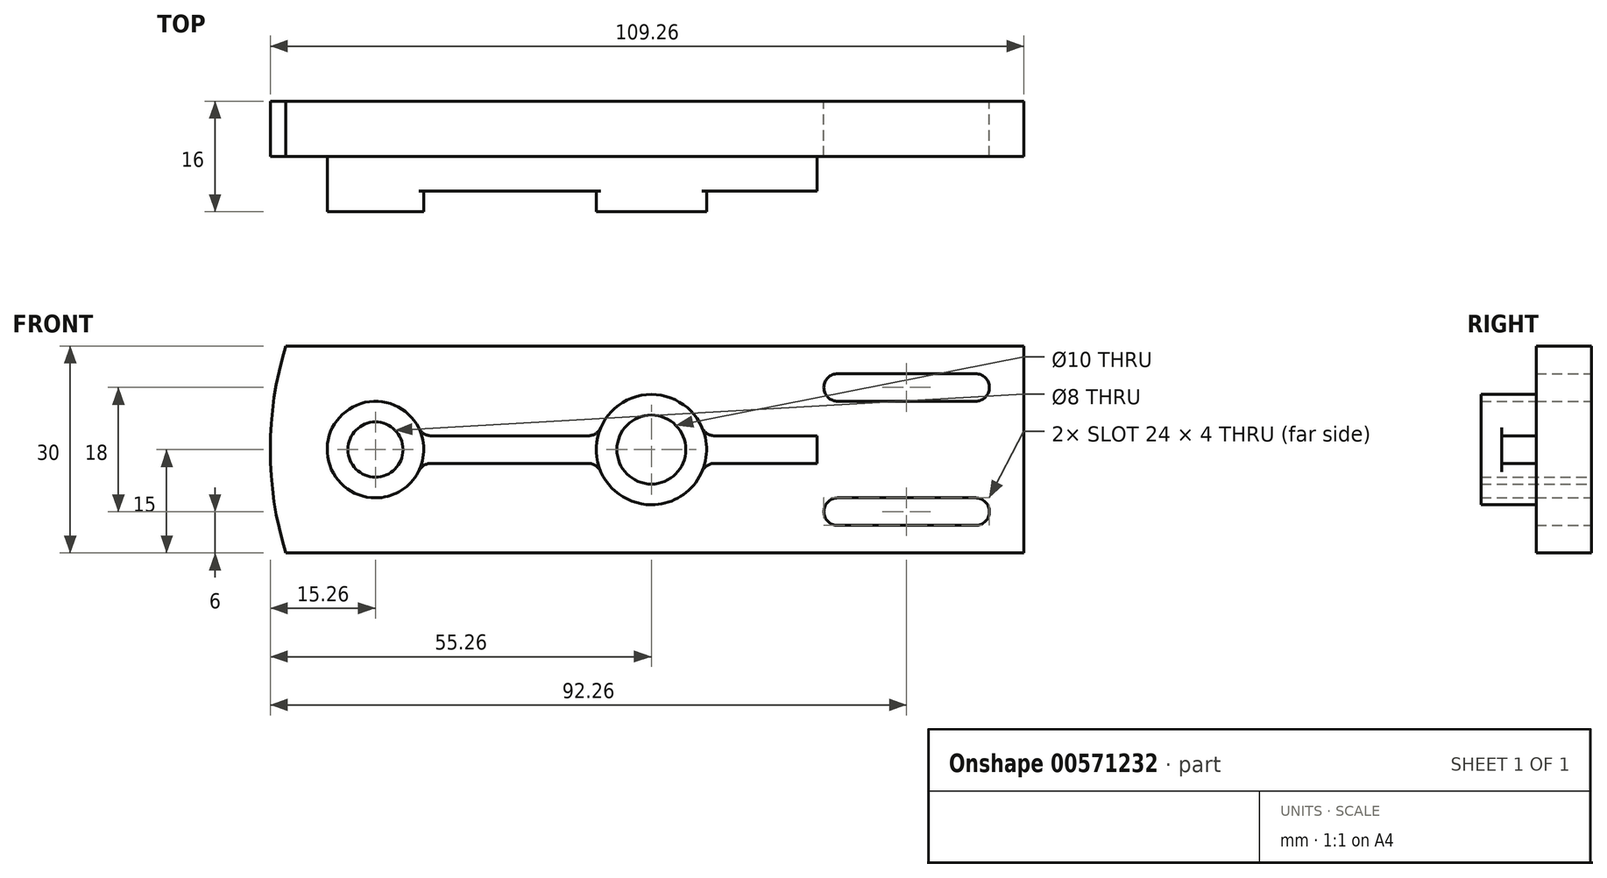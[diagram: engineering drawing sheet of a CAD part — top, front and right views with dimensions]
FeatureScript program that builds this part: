
annotation { "Feature Type Name" : "Feature", "Feature Type Description" : "" }
export const myFeature = defineFeature(function(context is Context, id is Id, definition is map)
    precondition{}
    {
        {
            var Q0;
            Q0=qCreatedBy(makeId("Front.planeOp"),FACE);
            var sketch = newSketch(context, id + "F0", { "sketchPlane" : qUnion([Q0])});
            skLineSegment(sketch, "E0", {"start": v(0, 0) * mm, "end": v(107, 0) * mm});
            skLineSegment(sketch, "E1", {"start": v(107, 0) * mm, "end": v(107, -30) * mm});
            skLineSegment(sketch, "E2", {"start": v(107, -30) * mm, "end": v(0, -30) * mm});
            skArc(sketch, "E3", {"start": v(0, 0) * mm, "mid": v(-2.26, -15) * mm, "end": v(0, -30) * mm});
            skLineSegment(sketch, "E4", {"start": v(-2.26, -15) * mm, "end": v(107, -15) * mm, "construction": true});
            skLineSegment(sketch, "E5", {"start": v(80, -4) * mm, "end": v(100, -4) * mm});
            skLineSegment(sketch, "E6", {"start": v(80, -8) * mm, "end": v(100, -8) * mm});
            skArc(sketch, "E7", {"start": v(100, -8) * mm, "mid": v(102, -6) * mm, "end": v(100, -4) * mm});
            skArc(sketch, "E8", {"start": v(80, -4) * mm, "mid": v(78, -6) * mm, "end": v(80, -8) * mm});
            skLineSegment(sketch, "E9", {"start": v(80, -22) * mm, "end": v(100, -22) * mm});
            skLineSegment(sketch, "E10", {"start": v(80, -26) * mm, "end": v(100, -26) * mm});
            skArc(sketch, "E11", {"start": v(100, -26) * mm, "mid": v(102, -24) * mm, "end": v(100, -22) * mm});
            skArc(sketch, "E12", {"start": v(80, -22) * mm, "mid": v(78, -24) * mm, "end": v(80, -26) * mm});
            skCircle(sketch, "E13", {"center": v(53, -15) * mm, "radius": 5 * mm});
            skCircle(sketch, "E14", {"center": v(13, -15) * mm, "radius": 4 * mm});
            skCircle(sketch, "E15", {"center": v(13, -15) * mm, "radius": 7 * mm});
            skCircle(sketch, "E16", {"center": v(53, -15) * mm, "radius": 8 * mm});
            skLineSegment(sketch, "E17.bottom", {"start": v(62.17, -13) * mm, "end": v(77, -13) * mm});
            skLineSegment(sketch, "E17.top", {"start": v(62.17, -17) * mm, "end": v(77, -17) * mm});
            skLineSegment(sketch, "E17.right", {"start": v(77, -13) * mm, "end": v(77, -17) * mm});
            skLineSegment(sketch, "E18", {"start": v(43.83, -13) * mm, "end": v(21.06, -13) * mm});
            skLineSegment(sketch, "E19", {"start": v(43.83, -17) * mm, "end": v(21.06, -17) * mm});
            skArc(sketch, "E20", {"start": v(19.27, -11.89) * mm, "mid": v(20, -12.7) * mm, "end": v(21.06, -13) * mm});
            skArc(sketch, "E21", {"start": v(21.06, -17) * mm, "mid": v(20, -17.3) * mm, "end": v(19.27, -18.11) * mm});
            skArc(sketch, "E22", {"start": v(43.83, -13) * mm, "mid": v(44.93, -12.67) * mm, "end": v(45.67, -11.8) * mm});
            skArc(sketch, "E23", {"start": v(60.33, -11.8) * mm, "mid": v(61.07, -12.67) * mm, "end": v(62.17, -13) * mm});
            skArc(sketch, "E24", {"start": v(62.17, -17) * mm, "mid": v(61.07, -17.33) * mm, "end": v(60.33, -18.2) * mm});
            skArc(sketch, "E25", {"start": v(45.67, -18.2) * mm, "mid": v(44.93, -17.33) * mm, "end": v(43.83, -17) * mm});
            skPoint(sketch, "E26.orphan", {"position": v(45.25, -13) * mm});
            skPoint(sketch, "E27.orphan", {"position": v(45.25, -17) * mm});
            skPoint(sketch, "E28.orphan", {"position": v(60.75, -13) * mm});
            skPoint(sketch, "E29.orphan", {"position": v(60.75, -17) * mm});
            skSolve(sketch);
        }
        {
            var Q0;
            Q0=makeQuery(id+"F0.imprint","IMPRINT",FACE,{"disambiguationData":[TD([[makeQuery(id+"F0.imprint","IMPRINT",EDGE,{"derivedFrom":sQuery(id+"F0.wireOp",EDGE,"E0")}),-1.0]])]});
            extrude(context, id + "F1", {"entities" : qUnion([Q0]), "depth" : 8 * mm, "offsetDistance" : 25 * mm});
        }
        {
            var Q0;
            Q0=makeQuery(id+"F0.imprint","IMPRINT",FACE,{"disambiguationData":[TD([[makeQuery(id+"F0.imprint","IMPRINT",EDGE,{"derivedFrom":sQuery(id+"F0.wireOp",EDGE,"E18")}),1.0]])]});
            var Q1;
            Q1=makeQuery(id+"F0.imprint","IMPRINT",FACE,{"disambiguationData":[TD([[makeQuery(id+"F0.imprint","IMPRINT",EDGE,{"derivedFrom":sQuery(id+"F0.wireOp",EDGE,"E17.bottom")}),-1.0]])]});
            extrude(context, id + "F2", {"entities" : qUnion([Q0, Q1]), "operationType" : NewBodyOperationType.ADD, "depth" : 13 * mm, "offsetDistance" : 25 * mm});
        }
        {
            var Q0;
            Q0=makeQuery(id+"F0.imprint","IMPRINT",FACE,{"disambiguationData":[TD([[makeQuery(id+"F0.imprint","IMPRINT",EDGE,{"derivedFrom":sQuery(id+"F0.wireOp",EDGE,"E14")}),-1.0]])]});
            var Q1;
            Q1=makeQuery(id+"F0.imprint","IMPRINT",FACE,{"disambiguationData":[TD([[makeQuery(id+"F0.imprint","IMPRINT",EDGE,{"derivedFrom":sQuery(id+"F0.wireOp",EDGE,"E13")}),-1.0]])]});
            extrude(context, id + "F3", {"entities" : qUnion([Q0, Q1]), "operationType" : NewBodyOperationType.ADD, "depth" : 16 * mm, "offsetDistance" : 25 * mm});
        }
    });
